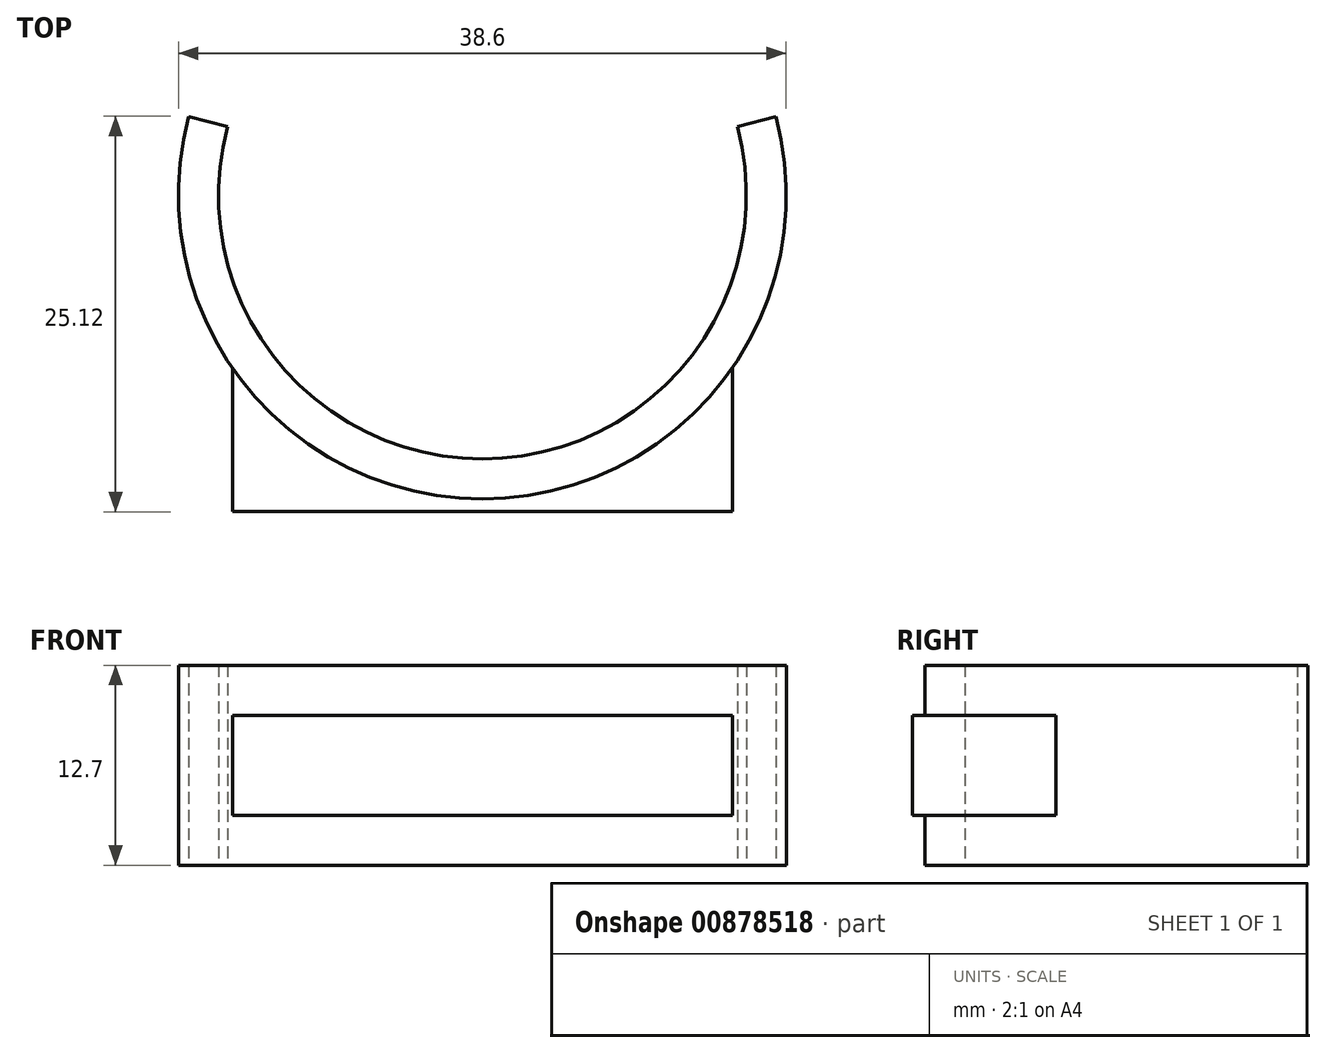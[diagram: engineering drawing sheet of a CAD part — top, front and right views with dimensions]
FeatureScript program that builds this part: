
annotation { "Feature Type Name" : "Feature", "Feature Type Description" : "" }
export const myFeature = defineFeature(function(context is Context, id is Id, definition is map)
    precondition{}
    {
        {
            var Q0;
            Q0=qCreatedBy(makeId("Top.planeOp"),FACE);
            var sketch = newSketch(context, id + "F0", { "sketchPlane" : qUnion([Q0])});
            skCircle(sketch, "E0", {"center": v(0, 0) * mm, "radius": 19.3 * mm});
            skCircle(sketch, "E1", {"center": v(0, 0) * mm, "radius": 16.76 * mm});
            skLineSegment(sketch, "E2", {"start": v(-53.94, 0) * mm, "end": v(51.47, 0) * mm, "construction": true});
            skLineSegment(sketch, "E3", {"start": v(0, 37.95) * mm, "end": v(0, -48.77) * mm, "construction": true});
            skLineSegment(sketch, "E4", {"start": v(0, 0) * mm, "end": v(-18.65, 5) * mm});
            skLineSegment(sketch, "E5.MirrorCS", {"start": v(0, 0) * mm, "end": v(18.65, 5) * mm});
            skLineSegment(sketch, "E6.top", {"start": v(-15.88, -20.12) * mm, "end": v(15.88, -20.12) * mm});
            skLineSegment(sketch, "E6.left", {"start": v(-15.87, -10.98) * mm, "end": v(-15.87, -20.12) * mm});
            skLineSegment(sketch, "E6.right", {"start": v(15.88, -10.98) * mm, "end": v(15.88, -20.12) * mm});
            skPoint(sketch, "E6.middle", {"position": v(0, -15.55) * mm});
            skSolve(sketch);
        }
        {
            var Q0;
            {var subQ0=sQuery(id+"F0.wireOp",EDGE,"E4");var subQ5=sQuery(id+"F0.wireOp",EDGE,"E0");var subQ9=makeQuery(id+"F0.imprint","INTERSECT",VERTEX,{"derivedFrom":[subQ5,subQ0]});Q0=makeQuery(id+"F0.imprint","IMPRINT",FACE,{"disambiguationData":[TD([[makeQuery(id+"F0.imprint","IMPRINT",EDGE,{"disambiguationData":[TD([[subQ9,-1.0]])],"derivedFrom":subQ5}),1.0]])]});}
            extrude(context, id + "F1", {"entities" : qUnion([Q0]), "endBound" : BoundingType.SYMMETRIC, "depth" : 12.7 * mm, "offsetDistance" : 25.4 * mm});
        }
        {
            var Q0;
            Q0=makeQuery(id+"F0.imprint","IMPRINT",FACE,{"disambiguationData":[TD([[makeQuery(id+"F0.imprint","IMPRINT",EDGE,{"derivedFrom":sQuery(id+"F0.wireOp",EDGE,"E6.top")}),1.0]])]});
            extrude(context, id + "F2", {"entities" : qUnion([Q0]), "operationType" : NewBodyOperationType.ADD, "endBound" : BoundingType.SYMMETRIC, "depth" : 6.35 * mm, "offsetDistance" : 25.4 * mm});
        }
    });
